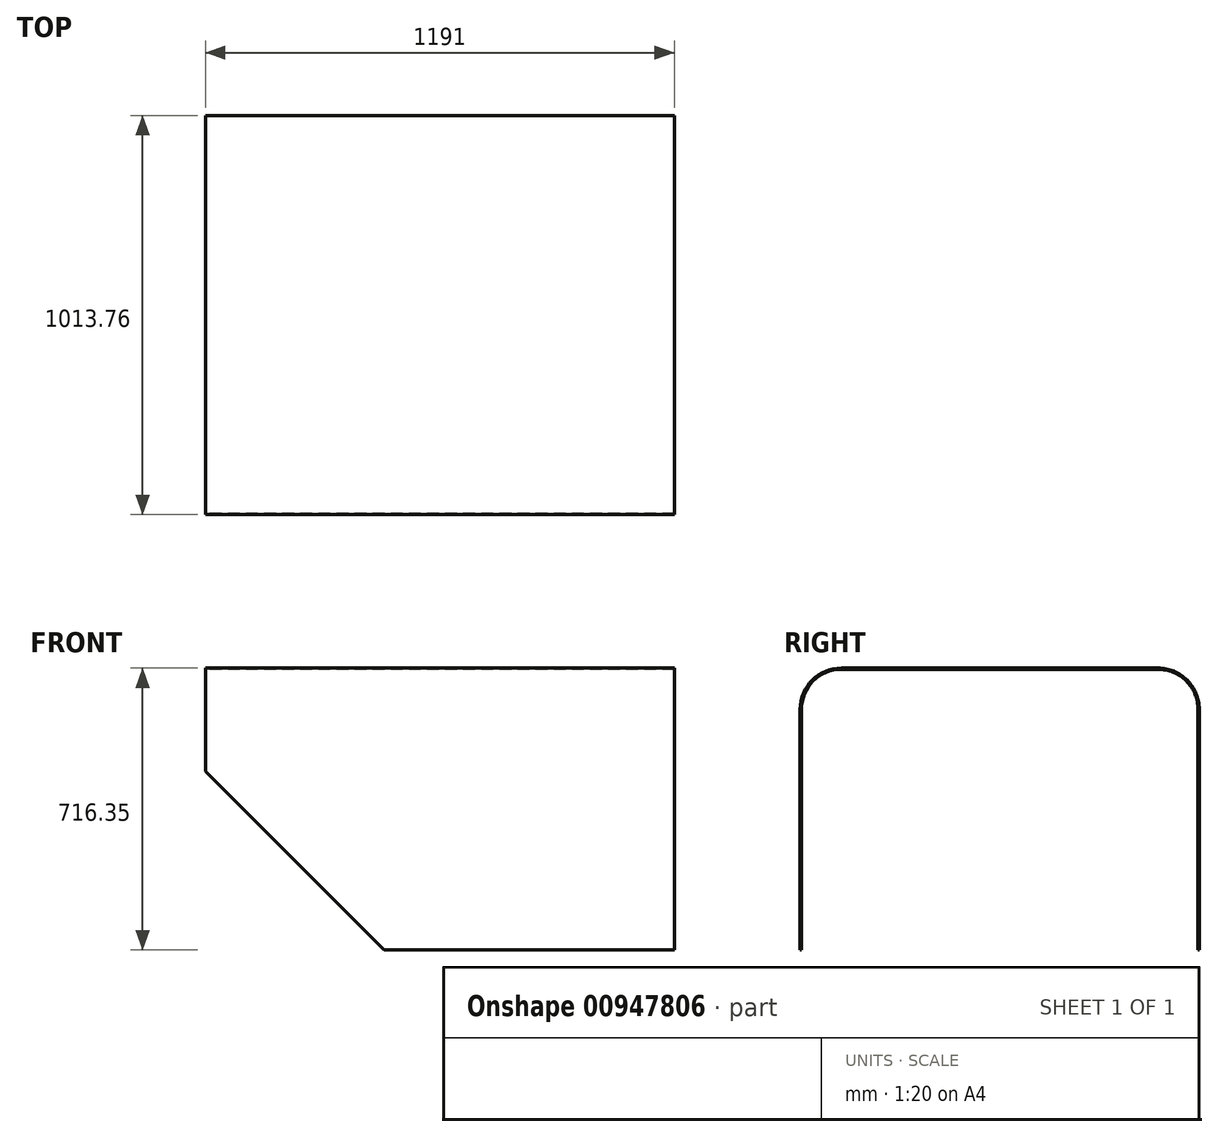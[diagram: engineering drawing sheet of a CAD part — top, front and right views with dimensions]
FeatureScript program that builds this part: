
annotation { "Feature Type Name" : "Feature", "Feature Type Description" : "" }
export const myFeature = defineFeature(function(context is Context, id is Id, definition is map)
    precondition{}
    {
        {
            var Q0;
            Q0=qCreatedBy(makeId("Right.planeOp"),FACE);
            var sketch = newSketch(context, id + "F0", { "sketchPlane" : qUnion([Q0])});
            skLineSegment(sketch, "E0", {"start": v(-503.7, -713.17) * mm, "end": v(-503.7, -101.6) * mm});
            skLineSegment(sketch, "E1", {"start": v(-402.1, 0) * mm, "end": v(402.1, 0) * mm});
            skLineSegment(sketch, "E2", {"start": v(503.7, -101.6) * mm, "end": v(503.7, -713.17) * mm});
            skPoint(sketch, "E3", {"position": v(402.1, 0) * mm});
            skArc(sketch, "E4", {"start": v(-503.7, -101.6) * mm, "mid": v(-473.94, -29.76) * mm, "end": v(-402.1, 0) * mm});
            skArc(sketch, "E5", {"start": v(402.1, 0) * mm, "mid": v(473.94, -29.76) * mm, "end": v(503.7, -101.6) * mm});
            skPoint(sketch, "E6", {"position": v(402.1, 3.17) * mm});
            skPoint(sketch, "E7", {"position": v(506.88, -101.6) * mm});
            skLineSegment(sketch, "E8", {"start": v(503.7, -713.17) * mm, "end": v(506.88, -713.17) * mm});
            skLineSegment(sketch, "E9", {"start": v(506.88, -713.17) * mm, "end": v(506.88, -101.6) * mm});
            skArc(sketch, "E10", {"start": v(506.88, -101.6) * mm, "mid": v(476.19, -27.51) * mm, "end": v(402.1, 3.17) * mm});
            skPoint(sketch, "E11", {"position": v(-402.1, 0) * mm});
            skPoint(sketch, "E12", {"position": v(-402.1, 3.17) * mm});
            skPoint(sketch, "E13", {"position": v(-506.88, -101.6) * mm});
            skLineSegment(sketch, "E14", {"start": v(402.1, 3.17) * mm, "end": v(-402.1, 3.17) * mm});
            skArc(sketch, "E15", {"start": v(-402.1, 3.17) * mm, "mid": v(-476.19, -27.51) * mm, "end": v(-506.88, -101.6) * mm});
            skLineSegment(sketch, "E16", {"start": v(-503.7, -713.17) * mm, "end": v(-506.88, -713.17) * mm});
            skLineSegment(sketch, "E17", {"start": v(-506.88, -713.17) * mm, "end": v(-506.88, -101.6) * mm});
            skPoint(sketch, "E18", {"position": v(0, 0) * mm});
            skSolve(sketch);
        }
        {
            var Q0;
            Q0 = qSketchRegion(id + "F0", true);
            extrude(context, id + "F1", {"entities" : qUnion([Q0]), "depth" : 1191 * mm, "offsetDistance" : 25 * mm});
        }
        {
            var Q0;
            Q0=makeQuery(id+"F1.opExtrude","SWEPT_FACE",FACE,{"disambiguationData":[OSD([sQuery(id+"F0.wireOp",EDGE,"E17")])]});
            var sketch = newSketch(context, id + "F2", { "sketchPlane" : qUnion([Q0])});
            skLineSegment(sketch, "E19", {"start": v(0, -259.91) * mm, "end": v(553.68, -813.6) * mm});
            skLineSegment(sketch, "E20", {"start": v(0, -259.91) * mm, "end": v(-226.74, -259.91) * mm});
            skLineSegment(sketch, "E21", {"start": v(-226.74, -259.91) * mm, "end": v(-226.74, -813.6) * mm});
            skLineSegment(sketch, "E22", {"start": v(-226.74, -813.6) * mm, "end": v(553.68, -813.6) * mm});
            skSolve(sketch);
        }
        {
            var Q0;
            Q0 = qSketchRegion(id + "F2", true);
            extrude(context, id + "F3", {"entities" : qUnion([Q0]), "operationType" : NewBodyOperationType.REMOVE, "endBound" : BoundingType.THROUGH_ALL, "oppositeDirection" : true, "depth" : 25 * mm, "offsetDistance" : 25 * mm});
        }
    });
